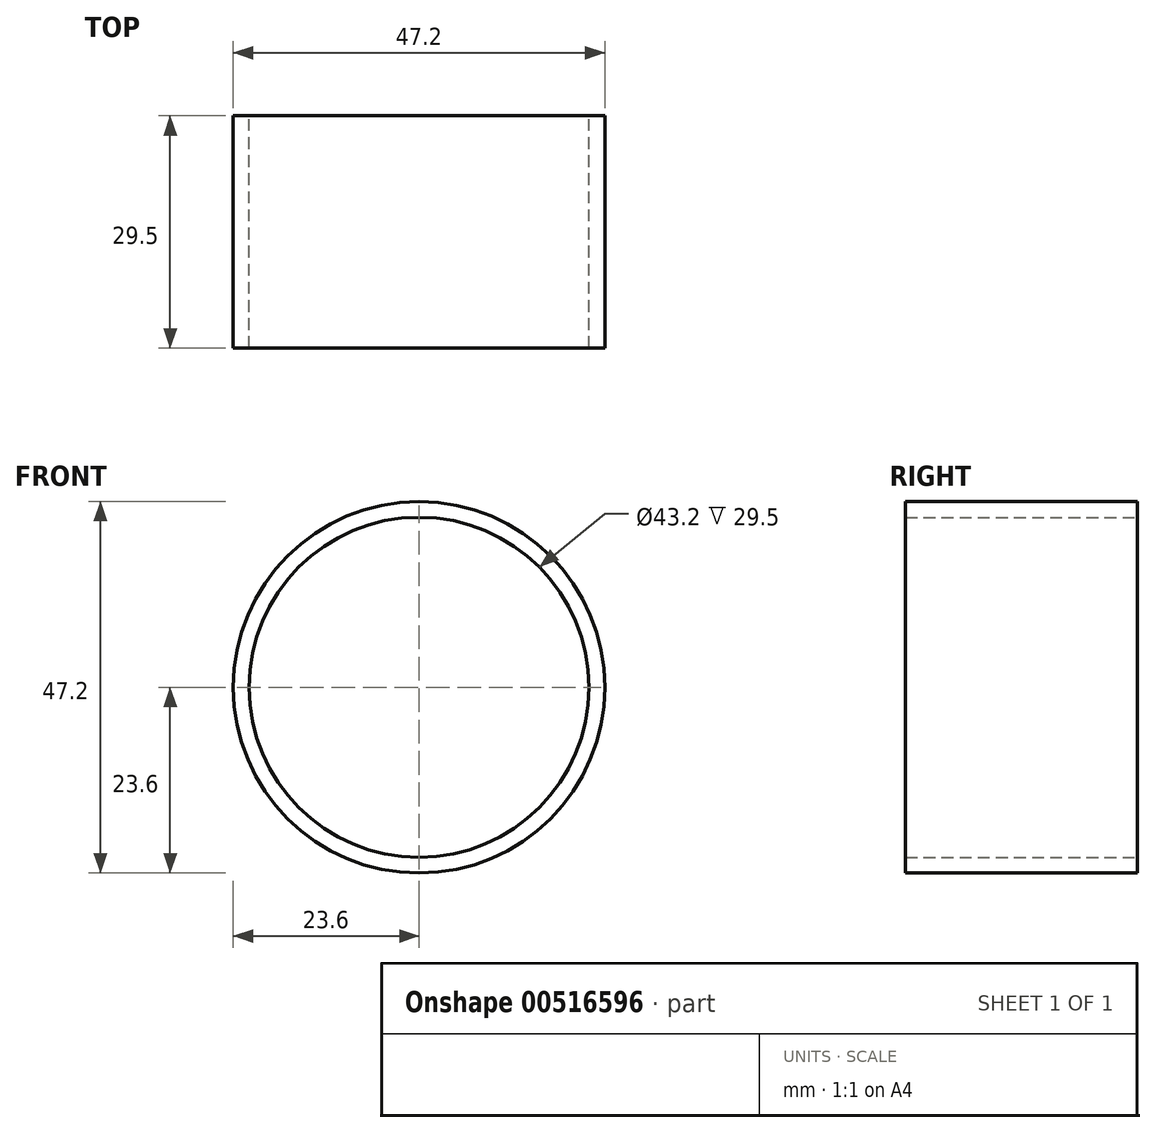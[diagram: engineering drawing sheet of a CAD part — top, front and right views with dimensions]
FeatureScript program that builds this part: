
annotation { "Feature Type Name" : "Feature", "Feature Type Description" : "" }
export const myFeature = defineFeature(function(context is Context, id is Id, definition is map)
    precondition{}
    {
        {
            var Q0;
            Q0=qCreatedBy(makeId("Front.planeOp"),FACE);
            var sketch = newSketch(context, id + "F0", { "sketchPlane" : qUnion([Q0])});
            skCircle(sketch, "E0", {"center": v(0, 0) * mm, "radius": 23.6 * mm});
            skCircle(sketch, "E1", {"center": v(0, 0) * mm, "radius": 21.6 * mm});
            skSolve(sketch);
        }
        {
            var Q0;
            Q0 = qSketchRegion(id + "F0", true);
            extrude(context, id + "F1", {"entities" : qUnion([Q0]), "endBound" : BoundingType.SYMMETRIC, "depth" : 29.5 * mm, "offsetDistance" : 25 * mm});
        }
    });
